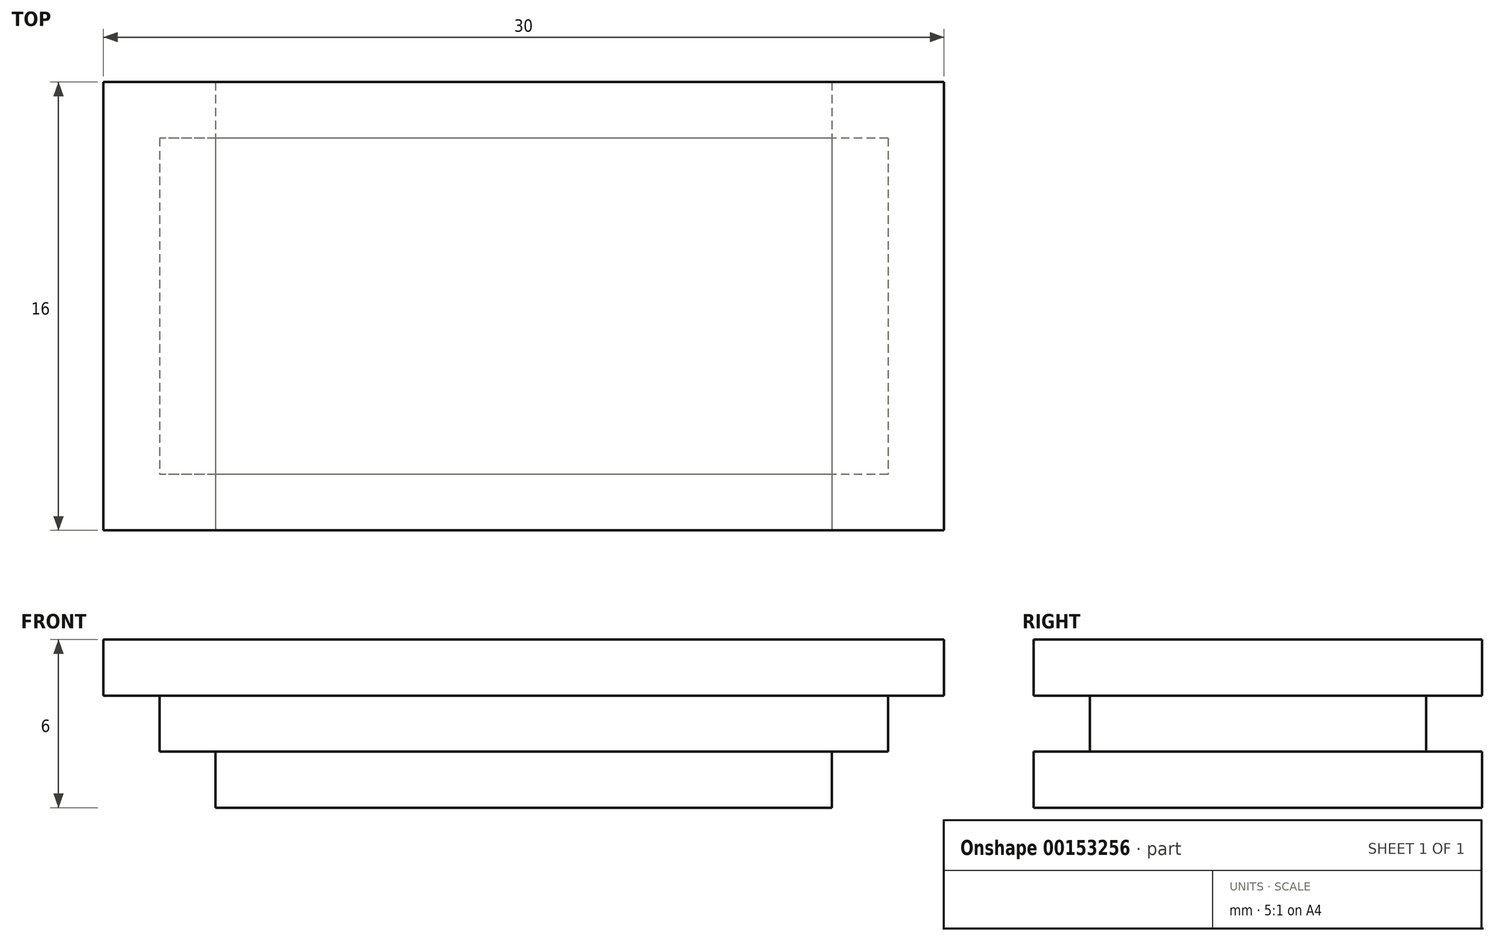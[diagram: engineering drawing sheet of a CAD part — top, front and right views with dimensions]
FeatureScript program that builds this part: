
annotation { "Feature Type Name" : "Feature", "Feature Type Description" : "" }
export const myFeature = defineFeature(function(context is Context, id is Id, definition is map)
    precondition{}
    {
        {
            assignVariable(context, id + "F0", {"name" : "T", "anyValue" : 2});
        }
        {
            var Q0;
            Q0=qCreatedBy(makeId("Top.planeOp"),FACE);
            var sketch = newSketch(context, id + "F1", { "sketchPlane" : qUnion([Q0])});
            skLineSegment(sketch, "E0.bottom", {"start": v(11, 8) * mm, "end": v(-11, 8) * mm});
            skLineSegment(sketch, "E0.top", {"start": v(11, -8) * mm, "end": v(-11, -8) * mm});
            skLineSegment(sketch, "E0.left", {"start": v(11, 8) * mm, "end": v(11, -8) * mm});
            skLineSegment(sketch, "E0.right", {"start": v(-11, 8) * mm, "end": v(-11, -8) * mm});
            skPoint(sketch, "E0.middle", {"position": v(0, 0) * mm});
            skSolve(sketch);
        }
        {
            var Q0;
            Q0=makeQuery(id+"F1.imprint","IMPRINT",FACE,{"disambiguationData":[TD([[makeQuery(id+"F1.imprint","IMPRINT",EDGE,{"derivedFrom":sQuery(id+"F1.wireOp",EDGE,"E0.bottom")}),1.0]])]});
            extrude(context, id + "F2", {"entities" : qUnion([Q0]), "depth" : (getVariable(context, 'T')) * mm});
        }
        {
            var Q0;
            Q0=makeQuery(id+"F2.opExtrude","CAP_FACE",FACE,{"disambiguationData":[OSD([sQuery(id+"F1.wireOp",EDGE,"E0.bottom"),sQuery(id+"F1.wireOp",EDGE,"E0.top"),sQuery(id+"F1.wireOp",EDGE,"E0.left"),sQuery(id+"F1.wireOp",EDGE,"E0.right")])],"isStart":false});
            var sketch = newSketch(context, id + "F3", { "sketchPlane" : qUnion([Q0])});
            skLineSegment(sketch, "E1.bottom", {"start": v(13, 6) * mm, "end": v(-13, 6) * mm});
            skLineSegment(sketch, "E1.top", {"start": v(13, -6) * mm, "end": v(-13, -6) * mm});
            skLineSegment(sketch, "E1.left", {"start": v(13, 6) * mm, "end": v(13, -6) * mm});
            skLineSegment(sketch, "E1.right", {"start": v(-13, 6) * mm, "end": v(-13, -6) * mm});
            skPoint(sketch, "E1.middle", {"position": v(0, 0) * mm});
            skSolve(sketch);
        }
        {
            var Q0;
            {var subQ0=sQuery(id+"F3.wireOp",EDGE,"E1.right");Q0=makeQuery(id+"F3.imprint","IMPRINT",FACE,{"disambiguationData":[TD([[makeQuery(id+"F3.imprint","IMPRINT",EDGE,{"derivedFrom":subQ0}),1.0]])]});}
            var Q1;
            {var subQ0=sQuery(id+"F3.wireOp",EDGE,"E1.bottom");var subQ1=makeQuery(id+"F2.opExtrude","CAP_EDGE",EDGE,{"disambiguationData":[OSD([sQuery(id+"F1.wireOp",EDGE,"E0.left")])],"isStart":false});var subQ2=makeQuery(id+"F3.imprint","INTERSECT",VERTEX,{"derivedFrom":[subQ1,subQ0]});Q1=makeQuery(id+"F3.imprint","IMPRINT",FACE,{"disambiguationData":[TD([[makeQuery(id+"F3.imprint","IMPRINT",EDGE,{"disambiguationData":[TD([[subQ2,-1.0]])],"derivedFrom":subQ0}),1.0]])]});}
            var Q2;
            {var subQ0=sQuery(id+"F3.wireOp",EDGE,"E1.left");Q2=makeQuery(id+"F3.imprint","IMPRINT",FACE,{"disambiguationData":[TD([[makeQuery(id+"F3.imprint","IMPRINT",EDGE,{"derivedFrom":subQ0}),-1.0]])]});}
            extrude(context, id + "F4", {"entities" : qUnion([Q0, Q1, Q2]), "operationType" : NewBodyOperationType.ADD, "depth" : (getVariable(context, 'T')) * mm});
        }
        {
            var Q0;
            Q0=makeQuery(id+"F4.opExtrude","CAP_FACE",FACE,{"disambiguationData":[OSD([sQuery(id+"F3.wireOp",EDGE,"E1.bottom"),sQuery(id+"F3.wireOp",EDGE,"E1.top"),sQuery(id+"F3.wireOp",EDGE,"E1.left"),sQuery(id+"F3.wireOp",EDGE,"E1.right")])],"isStart":false});
            var sketch = newSketch(context, id + "F5", { "sketchPlane" : qUnion([Q0])});
            skLineSegment(sketch, "E2.bottom", {"start": v(15, -8) * mm, "end": v(-15, -8) * mm});
            skLineSegment(sketch, "E2.top", {"start": v(15, 8) * mm, "end": v(-15, 8) * mm});
            skLineSegment(sketch, "E2.left", {"start": v(15, -8) * mm, "end": v(15, 8) * mm});
            skLineSegment(sketch, "E2.right", {"start": v(-15, -8) * mm, "end": v(-15, 8) * mm});
            skPoint(sketch, "E2.middle", {"position": v(0, 0) * mm});
            skSolve(sketch);
        }
        {
            var Q0;
            Q0=makeQuery(id+"F5.imprint","IMPRINT",FACE,{"disambiguationData":[TD([[makeQuery(id+"F5.imprint","IMPRINT",EDGE,{"derivedFrom":sQuery(id+"F5.wireOp",EDGE,"E2.bottom")}),-1.0]])]});
            var Q1;
            Q1=makeQuery(id+"F5.imprint","IMPRINT",FACE,{"disambiguationData":[TD([[makeQuery(id+"F5.imprint","IMPRINT",EDGE,{"derivedFrom":makeQuery(id+"F4.opExtrude","CAP_EDGE",EDGE,{"disambiguationData":[OSD([sQuery(id+"F3.wireOp",EDGE,"E1.bottom")])],"isStart":false})}),1.0]])]});
            extrude(context, id + "F6", {"entities" : qUnion([Q0, Q1]), "operationType" : NewBodyOperationType.ADD, "depth" : (getVariable(context, 'T')) * mm});
        }
    });
